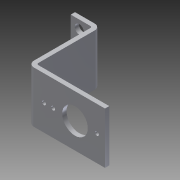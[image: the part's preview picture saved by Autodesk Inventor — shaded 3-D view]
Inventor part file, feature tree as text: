
AUTODESK INVENTOR PART (.ipt)
format: ipt  version: 2014 SP1 (Build 180222100, 222)  size: 222,208 bytes
history: native  units: in
note: dims shown in document units (in); Inventor stores cm internally (conversion verified against a paired STEP export)
features: other x7, sketch x6, sheet_metal_op x5, reference x4
ambient origin geometry x8: Origin, YZ Plane, XZ Plane, XY Plane, X Axis, Y Axis, Z Axis, Center Point
bodies: Solid1 (feature_tree)
feature tree (22):
  sheet_metal_op  "Face1"
  sheet_metal_op  "Flange1"
  sheet_metal_op  "Flange2"
  sketch  "Sketch1"  dims[d0=1.5in]
  other  "Plate1"
  sketch  "Sketch2"  dims[d1=0.75in]
  other  "Plate2"
  sheet_metal_op  "Bend1"
  sketch  "Sketch3"  dims[d2=0.266in]
  other  "Plate3"
  sheet_metal_op  "Bend2"
  sketch  "Sketch4"  dims[d3=0.266in]
  reference  "Reference1"
  sketch  "Sketch5"  dims[d4=1.0in]
  reference  "Reference2"
  reference  "Reference3"
  reference  "Reference4"
  sketch  "Sketch6"  dims[d5=0.25in d6=0.25in d7=0.25in d8=0.125in d9=0.125in d10=0.0625in d11=0.25in d12=0.125in d13=2.0in d14=90.0deg d15=0.05in d16=0.5in d17=0.125in d18=0.125in d19=0.125in d20=0.0625in d21=0.25in d22=0.125in d23=2.25in d24=90.0deg d25=0.05in d26=0.5in d27=0.125in d28=0.125in d29=0.5in d31=0.125in d32=0.0in d33=0.125in d34=0.0in d35=0.748in d36=0.125in d37=0.0in]
  other  "Cut1"
  other  "Cut2"
  other  "Cut3"
  other  "Definition1"
